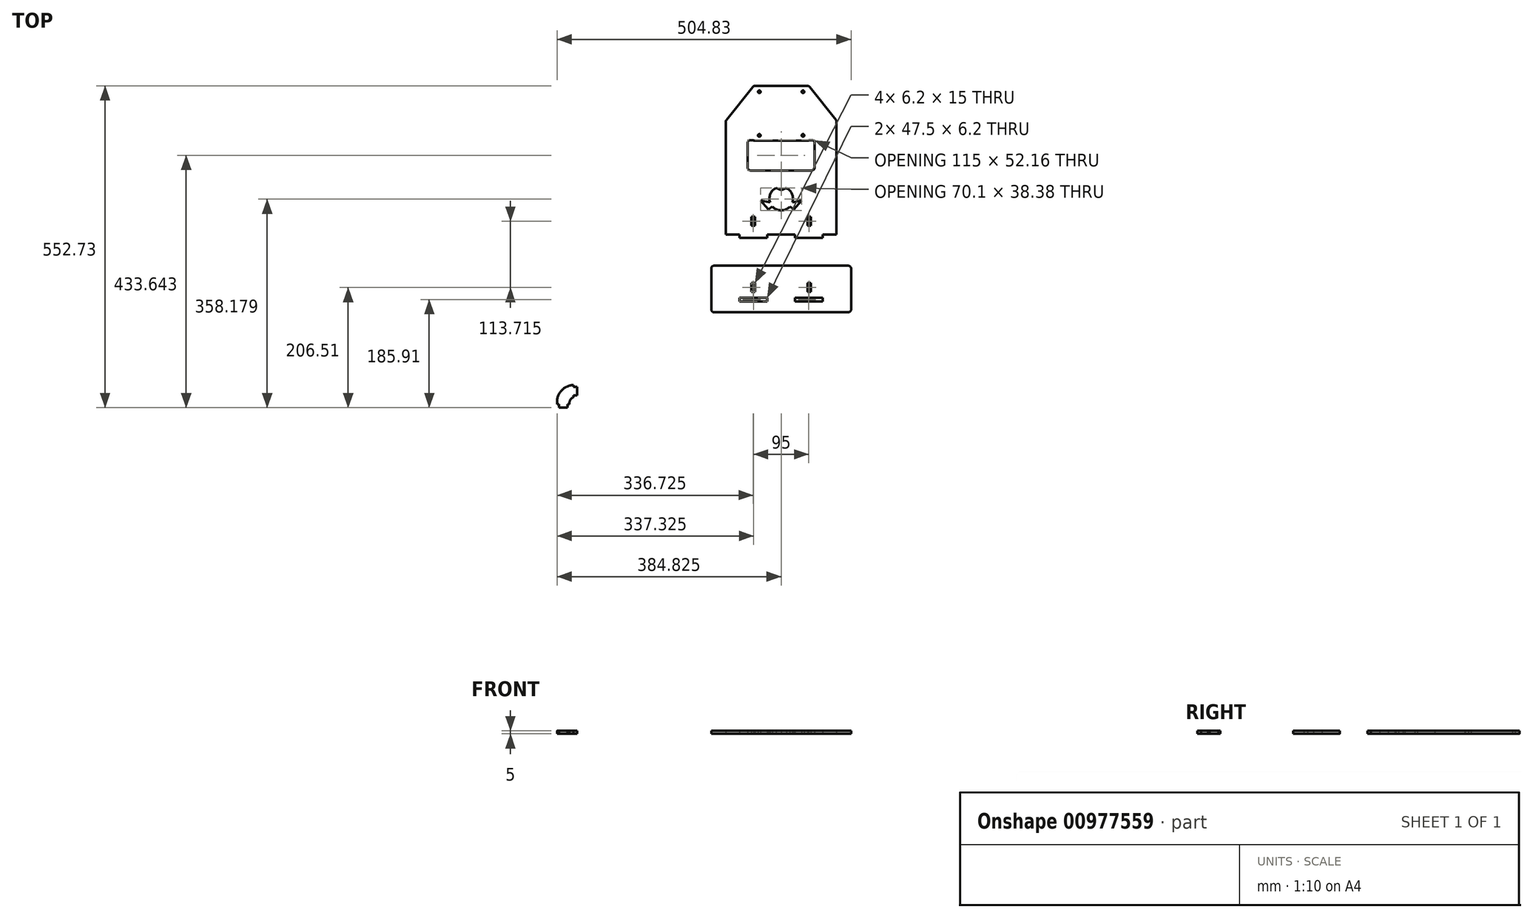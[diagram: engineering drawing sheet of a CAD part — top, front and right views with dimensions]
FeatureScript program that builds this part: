
annotation { "Feature Type Name" : "Feature", "Feature Type Description" : "" }
export const myFeature = defineFeature(function(context is Context, id is Id, definition is map)
    precondition{}
    {
        {
            var Q0;
            Q0=qCreatedBy(makeId("Top.planeOp"),FACE);
            var sketch = newSketch(context, id + "F0", { "sketchPlane" : qUnion([Q0])});
            skLineSegment(sketch, "E0.bottom", {"start": v(-60.37, 55.26) * mm, "end": v(-58.12, 55.26) * mm});
            skLineSegment(sketch, "E0.top", {"start": v(-60.37, -19.74) * mm, "end": v(-58.12, -19.74) * mm});
            skLineSegment(sketch, "E0.left", {"start": v(-60.37, 55.26) * mm, "end": v(-60.37, 53) * mm});
            skLineSegment(sketch, "E0.right", {"start": v(14.63, 55.26) * mm, "end": v(14.63, 53) * mm});
            skLineSegment(sketch, "E1", {"start": v(-22.87, -29.74) * mm, "end": v(-22.87, -75.74) * mm});
            skLineSegment(sketch, "E2", {"start": v(-22.87, -29.74) * mm, "end": v(-77.87, -29.74) * mm});
            skLineSegment(sketch, "E3", {"start": v(-77.87, -29.74) * mm, "end": v(32.13, -29.74) * mm});
            skLineSegment(sketch, "E4", {"start": v(32.13, -29.74) * mm, "end": v(32.13, -75.74) * mm});
            skLineSegment(sketch, "E5", {"start": v(32.13, -75.74) * mm, "end": v(-77.87, -75.74) * mm});
            skLineSegment(sketch, "E6", {"start": v(-77.87, -75.74) * mm, "end": v(-77.87, -29.74) * mm});
            skCircle(sketch, "E7", {"center": v(-60.37, 55.26) * mm, "radius": 2.25 * mm});
            skCircle(sketch, "E8", {"center": v(14.63, 55.26) * mm, "radius": 2.25 * mm});
            skCircle(sketch, "E9", {"center": v(14.63, -19.74) * mm, "radius": 2.25 * mm});
            skCircle(sketch, "E10", {"center": v(-60.37, -19.74) * mm, "radius": 2.25 * mm});
            skLineSegment(sketch, "E11.0", {"start": v(-60.37, 65.26) * mm, "end": v(14.63, 65.26) * mm});
            skLineSegment(sketch, "E12.0", {"start": v(-70.37, -27.74) * mm, "end": v(-70.37, -28.74) * mm});
            skLineSegment(sketch, "E12.1", {"start": v(-67.96, 65.26) * mm, "end": v(22.21, 65.26) * mm});
            skLineSegment(sketch, "E12.2", {"start": v(24.63, -27.74) * mm, "end": v(24.63, -28.74) * mm});
            skLineSegment(sketch, "E12.3", {"start": v(-70.37, -29.74) * mm, "end": v(24.63, -29.74) * mm});
            skLineSegment(sketch, "E13", {"start": v(-71.88, 63.37) * mm, "end": v(-116.79, 6.94) * mm});
            skLineSegment(sketch, "E14.MirrorCS", {"start": v(26.13, 63.37) * mm, "end": v(71.04, 6.94) * mm});
            skLineSegment(sketch, "E15", {"start": v(-70.37, -28.74) * mm, "end": v(-70.37, -27.74) * mm});
            skLineSegment(sketch, "E16", {"start": v(-70.37, -27.74) * mm, "end": v(-75.37, -27.74) * mm});
            skLineSegment(sketch, "E17", {"start": v(-80.37, -32.74) * mm, "end": v(-80.37, -74.9) * mm});
            skLineSegment(sketch, "E18", {"start": v(-117.87, -189.74) * mm, "end": v(-94.12, -189.74) * mm});
            skLineSegment(sketch, "E19.MirrorCS", {"start": v(24.63, -27.74) * mm, "end": v(29.63, -27.74) * mm});
            skLineSegment(sketch, "E20.MirrorCS", {"start": v(34.63, -32.74) * mm, "end": v(34.63, -74.9) * mm});
            skLineSegment(sketch, "E21.MirrorCS", {"start": v(72.13, -189.74) * mm, "end": v(48.38, -189.74) * mm});
            skLineSegment(sketch, "E22", {"start": v(-75.37, -79.9) * mm, "end": v(29.63, -79.9) * mm});
            skPoint(sketch, "E23.orphan", {"position": v(-88.33, -85.74) * mm});
            skPoint(sketch, "E24.end.orphan", {"position": v(-80.37, -85.74) * mm});
            skPoint(sketch, "E25.orphan", {"position": v(34.63, -85.74) * mm});
            skPoint(sketch, "E26.orphan", {"position": v(42.58, -85.74) * mm});
            skPoint(sketch, "E27.MirrorCS.start.orphan", {"position": v(-22.87, -85.74) * mm});
            skLineSegment(sketch, "E28", {"start": v(-70.37, -28.74) * mm, "end": v(24.63, -28.74) * mm});
            skLineSegment(sketch, "E29.trimOffspring", {"start": v(-60.37, -17.5) * mm, "end": v(-60.37, -19.74) * mm});
            skLineSegment(sketch, "E30.trimOffspring", {"start": v(12.38, 55.26) * mm, "end": v(14.63, 55.26) * mm});
            skLineSegment(sketch, "E31.trimOffspring", {"start": v(14.63, -17.5) * mm, "end": v(14.63, -19.74) * mm});
            skPoint(sketch, "E32.visualSharp", {"position": v(-153.82, -39.6) * mm});
            skPoint(sketch, "E33.visualSharp", {"position": v(-70.37, 65.26) * mm});
            skArc(sketch, "E33.filletArc", {"start": v(-67.96, 65.26) * mm, "mid": v(-70.14, 64.76) * mm, "end": v(-71.88, 63.37) * mm});
            skPoint(sketch, "E34.visualSharp", {"position": v(24.63, 65.26) * mm});
            skArc(sketch, "E34.filletArc", {"start": v(26.13, 63.37) * mm, "mid": v(24.39, 64.76) * mm, "end": v(22.21, 65.26) * mm});
            skPoint(sketch, "E35.visualSharp", {"position": v(108.08, -39.6) * mm});
            skPoint(sketch, "E36.visualSharp", {"position": v(-80.37, -27.74) * mm});
            skArc(sketch, "E36.filletArc", {"start": v(-75.37, -27.74) * mm, "mid": v(-78.91, -29.2) * mm, "end": v(-80.37, -32.74) * mm});
            skPoint(sketch, "E37.visualSharp", {"position": v(-80.37, -79.9) * mm});
            skArc(sketch, "E37.filletArc", {"start": v(-80.37, -74.9) * mm, "mid": v(-78.91, -78.44) * mm, "end": v(-75.37, -79.9) * mm});
            skPoint(sketch, "E38.visualSharp", {"position": v(34.63, -79.9) * mm});
            skArc(sketch, "E38.filletArc", {"start": v(29.63, -79.9) * mm, "mid": v(33.16, -78.44) * mm, "end": v(34.63, -74.9) * mm});
            skPoint(sketch, "E39.visualSharp", {"position": v(34.63, -27.74) * mm});
            skArc(sketch, "E39.filletArc", {"start": v(34.63, -32.74) * mm, "mid": v(33.16, -29.2) * mm, "end": v(29.63, -27.74) * mm});
            skLineSegment(sketch, "E40.trimOffspring", {"start": v(12.38, -19.74) * mm, "end": v(14.63, -19.74) * mm});
            skPoint(sketch, "E41.orphan", {"position": v(-22.87, -19.74) * mm});
            skLineSegment(sketch, "E42", {"start": v(-77.87, -52.74) * mm, "end": v(-80.37, -52.74) * mm});
            skLineSegment(sketch, "E43", {"start": v(-117.87, -52.74) * mm, "end": v(-117.87, 3.83) * mm});
            skLineSegment(sketch, "E44", {"start": v(-117.87, 5.58) * mm, "end": v(-117.87, -189.74) * mm});
            skPoint(sketch, "E45.orphan", {"position": v(-153.82, -189.74) * mm});
            skLineSegment(sketch, "E46.MirrorCS", {"start": v(72.13, -52.74) * mm, "end": v(72.13, 5.58) * mm});
            skLineSegment(sketch, "E47.MirrorCS", {"start": v(72.13, 3.83) * mm, "end": v(72.13, -189.74) * mm});
            skLineSegment(sketch, "E48", {"start": v(-22.87, -189.74) * mm, "end": v(-22.87, -243.46) * mm});
            skLineSegment(sketch, "E49", {"start": v(-22.87, -243.46) * mm, "end": v(-137.87, -243.46) * mm});
            skLineSegment(sketch, "E50", {"start": v(-22.87, -243.46) * mm, "end": v(92.13, -243.46) * mm});
            skLineSegment(sketch, "E51", {"start": v(97.13, -248.46) * mm, "end": v(97.13, -318.46) * mm});
            skLineSegment(sketch, "E52", {"start": v(92.13, -323.46) * mm, "end": v(-137.87, -323.46) * mm});
            skLineSegment(sketch, "E53", {"start": v(-142.87, -318.46) * mm, "end": v(-142.87, -248.46) * mm});
            skLineSegment(sketch, "E54", {"start": v(-94.12, -189.74) * mm, "end": v(-94.12, -194.74) * mm});
            skLineSegment(sketch, "E55.MirrorCS", {"start": v(-46.62, -189.74) * mm, "end": v(-46.62, -194.74) * mm});
            skLineSegment(sketch, "E56.MirrorCS", {"start": v(48.38, -189.74) * mm, "end": v(48.38, -194.74) * mm});
            skLineSegment(sketch, "E57.MirrorCS", {"start": v(0.88, -189.74) * mm, "end": v(0.88, -194.74) * mm});
            skPoint(sketch, "E58.start.orphan", {"position": v(24.63, -189.74) * mm});
            skLineSegment(sketch, "E59", {"start": v(-142.87, -283.46) * mm, "end": v(-142.87, -298.46) * mm});
            skLineSegment(sketch, "E60", {"start": v(-94.12, -298.46) * mm, "end": v(-46.62, -298.46) * mm});
            skLineSegment(sketch, "E61", {"start": v(-94.12, -298.46) * mm, "end": v(-94.12, -303.46) * mm});
            skLineSegment(sketch, "E62", {"start": v(-46.62, -303.46) * mm, "end": v(-46.62, -298.46) * mm});
            skLineSegment(sketch, "E63.MirrorCS", {"start": v(0.88, -303.46) * mm, "end": v(0.88, -298.46) * mm});
            skLineSegment(sketch, "E64.MirrorCS", {"start": v(48.38, -298.46) * mm, "end": v(48.38, -303.46) * mm});
            skLineSegment(sketch, "E65.trimOffspring", {"start": v(0.88, -298.46) * mm, "end": v(48.38, -298.46) * mm});
            skPoint(sketch, "E66.end.orphan", {"position": v(97.13, -283.46) * mm});
            skLineSegment(sketch, "E67.trimOffspring", {"start": v(-46.62, -189.74) * mm, "end": v(-22.87, -189.74) * mm});
            skLineSegment(sketch, "E68.trimOffspring", {"start": v(0.88, -189.74) * mm, "end": v(-22.87, -189.74) * mm});
            skPoint(sketch, "E69.orphan", {"position": v(-70.37, -189.74) * mm});
            skPoint(sketch, "E70.visualSharp", {"position": v(-117.87, 5.58) * mm});
            skArc(sketch, "E70.filletArc", {"start": v(-116.79, 6.94) * mm, "mid": v(-117.6, 5.48) * mm, "end": v(-117.87, 3.83) * mm});
            skPoint(sketch, "E71.visualSharp", {"position": v(72.13, 5.58) * mm});
            skArc(sketch, "E71.filletArc", {"start": v(72.13, 3.83) * mm, "mid": v(71.85, 5.48) * mm, "end": v(71.04, 6.94) * mm});
            skLineSegment(sketch, "E72.bottom", {"start": v(-418.38, -158.65) * mm, "end": v(-365.35, -158.65) * mm});
            skLineSegment(sketch, "E72.top", {"start": v(-418.38, -218.27) * mm, "end": v(-365.35, -218.27) * mm});
            skLineSegment(sketch, "E72.left", {"start": v(-418.38, -158.65) * mm, "end": v(-418.38, -218.27) * mm});
            skLineSegment(sketch, "E72.right", {"start": v(-365.35, -158.65) * mm, "end": v(-365.35, -218.27) * mm});
            skLineSegment(sketch, "E73", {"start": v(-70.37, -159.74) * mm, "end": v(-72.87, -159.74) * mm});
            skLineSegment(sketch, "E74", {"start": v(-72.87, -159.74) * mm, "end": v(-67.87, -159.74) * mm});
            skPoint(sketch, "E74.endSnap0", {"position": v(-71.62, -159.74) * mm});
            skLineSegment(sketch, "E75", {"start": v(-72.87, -174.74) * mm, "end": v(-67.87, -174.74) * mm});
            skLineSegment(sketch, "E76", {"start": v(-67.87, -174.74) * mm, "end": v(-67.87, -159.74) * mm});
            skLineSegment(sketch, "E77", {"start": v(-365.35, -218.27) * mm, "end": v(-365.35, -203.27) * mm});
            skLineSegment(sketch, "E78", {"start": v(-365.35, -203.27) * mm, "end": v(-370.35, -203.27) * mm});
            skLineSegment(sketch, "E79", {"start": v(-370.35, -203.27) * mm, "end": v(-370.35, -218.27) * mm});
            skLineSegment(sketch, "E80", {"start": v(-365.35, -203.27) * mm, "end": v(-365.35, -188.27) * mm});
            skLineSegment(sketch, "E81", {"start": v(-70.37, -273.46) * mm, "end": v(-72.87, -273.46) * mm});
            skLineSegment(sketch, "E82", {"start": v(-72.87, -273.46) * mm, "end": v(-67.87, -273.46) * mm});
            skLineSegment(sketch, "E83", {"start": v(-67.87, -273.46) * mm, "end": v(-67.87, -288.46) * mm});
            skLineSegment(sketch, "E84", {"start": v(-67.87, -288.46) * mm, "end": v(-72.87, -288.46) * mm});
            skLineSegment(sketch, "E85.bottom", {"start": v(-379.42, -451.47) * mm, "end": v(-374.42, -451.47) * mm});
            skLineSegment(sketch, "E85.top", {"start": v(-379.42, -466.47) * mm, "end": v(-374.42, -466.47) * mm});
            skLineSegment(sketch, "E86", {"start": v(-389.42, -481.47) * mm, "end": v(-389.42, -486.47) * mm});
            skLineSegment(sketch, "E87", {"start": v(-404.42, -486.47) * mm, "end": v(-404.42, -481.47) * mm});
            skLineSegment(sketch, "E88", {"start": v(-379.42, -466.47) * mm, "end": v(-379.42, -469.47) * mm});
            skLineSegment(sketch, "E89", {"start": v(-379.42, -451.47) * mm, "end": v(-379.42, -448.47) * mm});
            skLineSegment(sketch, "E90", {"start": v(-389.42, -481.47) * mm, "end": v(-386.42, -481.47) * mm});
            skLineSegment(sketch, "E91", {"start": v(-404.42, -481.47) * mm, "end": v(-407.42, -481.47) * mm});
            skArc(sketch, "E92", {"start": v(-379.42, -448.47) * mm, "mid": v(-400.82, -458.7) * mm, "end": v(-407.42, -481.47) * mm});
            skArc(sketch, "E93", {"start": v(-379.42, -469.47) * mm, "mid": v(-384.98, -474.27) * mm, "end": v(-386.42, -481.47) * mm});
            skPoint(sketch, "E94.start.orphan", {"position": v(-70.37, -298.46) * mm});
            skPoint(sketch, "E95.start.orphan", {"position": v(-70.37, -288.46) * mm});
            skPoint(sketch, "E96.end.orphan", {"position": v(-70.37, -174.74) * mm});
            skLineSegment(sketch, "E97.MirrorCS", {"start": v(24.63, -159.74) * mm, "end": v(27.13, -159.74) * mm});
            skPoint(sketch, "E98.MirrorP", {"position": v(24.63, -174.74) * mm});
            skLineSegment(sketch, "E99.MirrorCS", {"start": v(27.13, -174.74) * mm, "end": v(22.13, -174.74) * mm});
            skLineSegment(sketch, "E100.MirrorCS", {"start": v(22.13, -174.74) * mm, "end": v(22.13, -159.74) * mm});
            skPoint(sketch, "E101.MirrorP", {"position": v(25.88, -159.74) * mm});
            skLineSegment(sketch, "E102.MirrorCS", {"start": v(27.13, -159.74) * mm, "end": v(22.13, -159.74) * mm});
            skLineSegment(sketch, "E103.MirrorCS", {"start": v(24.63, -273.46) * mm, "end": v(27.13, -273.46) * mm});
            skLineSegment(sketch, "E104.MirrorCS", {"start": v(22.13, -288.46) * mm, "end": v(27.13, -288.46) * mm});
            skLineSegment(sketch, "E105.MirrorCS", {"start": v(27.13, -273.46) * mm, "end": v(22.13, -273.46) * mm});
            skLineSegment(sketch, "E106.MirrorCS", {"start": v(22.13, -273.46) * mm, "end": v(22.13, -288.46) * mm});
            skPoint(sketch, "E107.MirrorP", {"position": v(24.63, -288.46) * mm});
            skPoint(sketch, "E108.visualSharp", {"position": v(97.13, -323.46) * mm});
            skArc(sketch, "E108.filletArc", {"start": v(92.13, -323.46) * mm, "mid": v(95.66, -322) * mm, "end": v(97.13, -318.46) * mm});
            skPoint(sketch, "E109.visualSharp", {"position": v(97.13, -243.46) * mm});
            skArc(sketch, "E109.filletArc", {"start": v(97.13, -248.46) * mm, "mid": v(95.66, -244.92) * mm, "end": v(92.13, -243.46) * mm});
            skPoint(sketch, "E110.visualSharp", {"position": v(-142.87, -323.46) * mm});
            skArc(sketch, "E110.filletArc", {"start": v(-142.87, -318.46) * mm, "mid": v(-141.41, -322) * mm, "end": v(-137.87, -323.46) * mm});
            skPoint(sketch, "E111.visualSharp", {"position": v(-142.87, -243.46) * mm});
            skArc(sketch, "E111.filletArc", {"start": v(-137.87, -243.46) * mm, "mid": v(-141.41, -244.92) * mm, "end": v(-142.87, -248.46) * mm});
            skArc(sketch, "E112", {"start": v(-31.8, -110.1) * mm, "mid": v(-22.87, -148.48) * mm, "end": v(-13.96, -110.1) * mm});
            skLineSegment(sketch, "E113", {"start": v(-37.73, -141.98) * mm, "end": v(-44.86, -146.6) * mm});
            skLineSegment(sketch, "E114", {"start": v(-44.86, -146.6) * mm, "end": v(-57.92, -131.4) * mm});
            skLineSegment(sketch, "E115", {"start": v(-57.92, -131.4) * mm, "end": v(-41.96, -134.95) * mm});
            skLineSegment(sketch, "E116.MirrorCS", {"start": v(-8.02, -141.98) * mm, "end": v(-0.89, -146.6) * mm});
            skLineSegment(sketch, "E117.MirrorCS", {"start": v(-0.89, -146.6) * mm, "end": v(12.18, -131.4) * mm});
            skLineSegment(sketch, "E118.MirrorCS", {"start": v(12.18, -131.4) * mm, "end": v(-3.79, -134.95) * mm});
            skLineSegment(sketch, "E119", {"start": v(-67.87, -159.74) * mm, "end": v(-74.07, -159.74) * mm});
            skLineSegment(sketch, "E120", {"start": v(-74.07, -159.74) * mm, "end": v(-74.07, -174.74) * mm});
            skLineSegment(sketch, "E121", {"start": v(-74.07, -174.74) * mm, "end": v(-72.87, -174.74) * mm});
            skLineSegment(sketch, "E122", {"start": v(-67.87, -273.46) * mm, "end": v(-74.07, -273.46) * mm});
            skLineSegment(sketch, "E123", {"start": v(-74.07, -273.46) * mm, "end": v(-74.07, -288.46) * mm});
            skLineSegment(sketch, "E124", {"start": v(-74.07, -288.46) * mm, "end": v(-72.87, -288.46) * mm});
            skLineSegment(sketch, "E125", {"start": v(-94.12, -189.74) * mm, "end": v(-94.12, -195.74) * mm});
            skLineSegment(sketch, "E126", {"start": v(-94.12, -195.74) * mm, "end": v(-46.62, -195.74) * mm});
            skLineSegment(sketch, "E127", {"start": v(48.38, -195.74) * mm, "end": v(48.38, -194.74) * mm});
            skLineSegment(sketch, "E128", {"start": v(0.88, -194.74) * mm, "end": v(0.88, -195.74) * mm});
            skLineSegment(sketch, "E129", {"start": v(-46.62, -194.74) * mm, "end": v(-46.62, -195.74) * mm});
            skPoint(sketch, "E130.MirrorCS.start.orphan", {"position": v(48.38, -194.74) * mm});
            skLineSegment(sketch, "E131.trimOffspring", {"start": v(0.88, -195.74) * mm, "end": v(48.38, -195.74) * mm});
            skLineSegment(sketch, "E132", {"start": v(-94.12, -298.46) * mm, "end": v(-94.12, -304.66) * mm});
            skLineSegment(sketch, "E133", {"start": v(-94.12, -304.66) * mm, "end": v(-46.62, -304.66) * mm});
            skLineSegment(sketch, "E134", {"start": v(-46.62, -304.66) * mm, "end": v(-46.62, -303.46) * mm});
            skLineSegment(sketch, "E135.MirrorCS", {"start": v(22.13, -273.46) * mm, "end": v(28.33, -273.46) * mm});
            skLineSegment(sketch, "E136.MirrorCS", {"start": v(28.33, -273.46) * mm, "end": v(28.33, -288.46) * mm});
            skLineSegment(sketch, "E137.MirrorCS", {"start": v(28.33, -288.46) * mm, "end": v(27.13, -288.46) * mm});
            skLineSegment(sketch, "E138.MirrorCS", {"start": v(48.38, -298.46) * mm, "end": v(48.38, -304.66) * mm});
            skLineSegment(sketch, "E139.MirrorCS", {"start": v(48.38, -304.66) * mm, "end": v(0.88, -304.66) * mm});
            skLineSegment(sketch, "E140.MirrorCS", {"start": v(0.88, -304.66) * mm, "end": v(0.88, -303.46) * mm});
            skLineSegment(sketch, "E141.MirrorCS", {"start": v(28.33, -174.74) * mm, "end": v(27.13, -174.74) * mm});
            skLineSegment(sketch, "E142.MirrorCS", {"start": v(28.33, -159.74) * mm, "end": v(28.33, -174.74) * mm});
            skLineSegment(sketch, "E143.MirrorCS", {"start": v(22.13, -159.74) * mm, "end": v(28.33, -159.74) * mm});
            skPoint(sketch, "E144.MirrorCS.end.orphan", {"position": v(0.88, -303.46) * mm});
            skPoint(sketch, "E144.MirrorCS.start.orphan", {"position": v(48.38, -303.46) * mm});
            skLineSegment(sketch, "E145", {"start": v(-379.42, -451.47) * mm, "end": v(-373.42, -451.47) * mm});
            skLineSegment(sketch, "E146", {"start": v(-373.42, -451.47) * mm, "end": v(-373.42, -466.47) * mm});
            skLineSegment(sketch, "E147", {"start": v(-373.42, -466.47) * mm, "end": v(-374.42, -466.47) * mm});
            skLineSegment(sketch, "E148", {"start": v(-404.42, -486.47) * mm, "end": v(-404.42, -487.47) * mm});
            skLineSegment(sketch, "E149", {"start": v(-404.42, -487.47) * mm, "end": v(-389.42, -487.47) * mm});
            skLineSegment(sketch, "E150", {"start": v(-389.42, -487.47) * mm, "end": v(-389.42, -486.47) * mm});
            skLineSegment(sketch, "E151", {"start": v(-22.87, -114) * mm, "end": v(-31.8, -110.1) * mm});
            skLineSegment(sketch, "E152.MirrorCS", {"start": v(-22.87, -114) * mm, "end": v(-13.96, -110.1) * mm});
            skSolve(sketch);
        }
        {
            var Q0;
            Q0=makeQuery(id+"F0.imprint","IMPRINT",FACE,{"disambiguationData":[TD([[makeQuery(id+"F0.imprint","IMPRINT",EDGE,{"derivedFrom":sQuery(id+"F0.wireOp",EDGE,"E12.2")}),-1.0]])]});
            var Q1;
            {var subQ10=sQuery(id+"F0.wireOp",EDGE,"E49");Q1=makeQuery(id+"F0.imprint","IMPRINT",FACE,{"disambiguationData":[TD([[makeQuery(id+"F0.imprint","IMPRINT",EDGE,{"derivedFrom":subQ10}),1.0]])]});}
            var Q2;
            Q2=makeQuery(id+"F0.imprint","IMPRINT",FACE,{"disambiguationData":[TD([[makeQuery(id+"F0.imprint","IMPRINT",EDGE,{"derivedFrom":sQuery(id+"F0.wireOp",EDGE,"E85.bottom")}),-1.0]])]});
            extrude(context, id + "F1", {"entities" : qUnion([Q0, Q1, Q2]), "depth" : 5 * mm, "offsetDistance" : 25 * mm});
        }
    });
